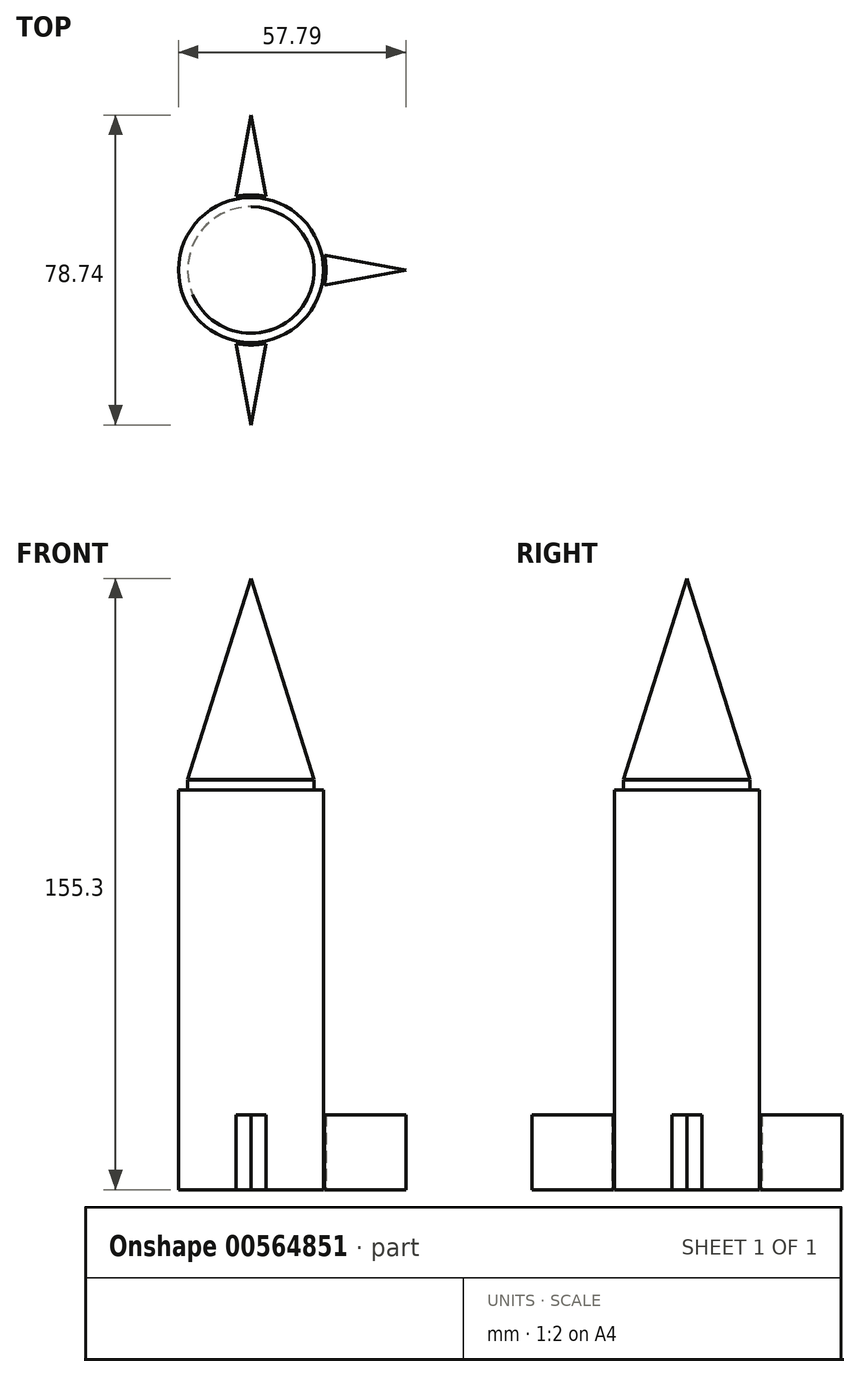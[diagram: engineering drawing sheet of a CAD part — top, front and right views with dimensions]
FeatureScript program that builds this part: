
annotation { "Feature Type Name" : "Feature", "Feature Type Description" : "" }
export const myFeature = defineFeature(function(context is Context, id is Id, definition is map)
    precondition{}
    {
        {
            var Q0;
            Q0=qCreatedBy(makeId("Top.planeOp"),FACE);
            var sketch = newSketch(context, id + "F0", { "sketchPlane" : qUnion([Q0])});
            skCircle(sketch, "E0", {"center": v(0, 0) * mm, "radius": 19.05 * mm});
            skPoint(sketch, "E1", {"position": v(-18.67, 3.81) * mm});
            skPoint(sketch, "E2", {"position": v(-18.67, -3.81) * mm});
            skPoint(sketch, "E3", {"position": v(-19.05, 0) * mm});
            skPoint(sketch, "E4", {"position": v(-39.37, 0) * mm});
            skLineSegment(sketch, "E5", {"start": v(-18.67, -3.8) * mm, "end": v(-39.37, 0) * mm});
            skLineSegment(sketch, "E6", {"start": v(-18.67, 3.8) * mm, "end": v(-39.37, 0) * mm});
            skPoint(sketch, "E7", {"position": v(-3.81, -18.67) * mm});
            skPoint(sketch, "E8", {"position": v(3.81, -18.67) * mm});
            skPoint(sketch, "E9", {"position": v(0, -19.05) * mm});
            skPoint(sketch, "E10", {"position": v(0, -39.37) * mm});
            skLineSegment(sketch, "E11", {"start": v(-3.81, -18.67) * mm, "end": v(0, -39.37) * mm});
            skLineSegment(sketch, "E12", {"start": v(3.81, -18.67) * mm, "end": v(0, -39.37) * mm});
            skLineSegment(sketch, "E13.MirrorCS", {"start": v(-18.67, 3.81) * mm, "end": v(-39.37, 0) * mm});
            skLineSegment(sketch, "E14.MirrorCS", {"start": v(-18.67, -3.81) * mm, "end": v(-39.37, 0) * mm});
            skLineSegment(sketch, "E15.MirrorCS", {"start": v(-3.81, 18.67) * mm, "end": v(0, 39.37) * mm});
            skLineSegment(sketch, "E16.MirrorCS", {"start": v(3.81, 18.67) * mm, "end": v(0, 39.37) * mm});
            skPoint(sketch, "E17.MirrorP", {"position": v(-3.81, 18.67) * mm});
            skPoint(sketch, "E18.MirrorP", {"position": v(0, 19.05) * mm});
            skPoint(sketch, "E19.MirrorP", {"position": v(3.81, 18.67) * mm});
            skPoint(sketch, "E20.MirrorP", {"position": v(0, 39.37) * mm});
            skLineSegment(sketch, "E21.MirrorCS", {"start": v(18.67, 3.81) * mm, "end": v(39.37, 0) * mm});
            skLineSegment(sketch, "E22.MirrorCS", {"start": v(18.67, -3.81) * mm, "end": v(39.37, 0) * mm});
            skPoint(sketch, "E23.MirrorP", {"position": v(39.37, 0) * mm});
            skPoint(sketch, "E24.MirrorP", {"position": v(18.67, 3.81) * mm});
            skPoint(sketch, "E25.MirrorP", {"position": v(19.05, 0) * mm});
            skPoint(sketch, "E26", {"position": v(18.67, -3.81) * mm});
            skSolve(sketch);
        }
        {
            var Q0;
            {var subQ0=sQuery(id+"F0.wireOp",EDGE,"E14.MirrorCS");Q0=makeQuery(id+"F0.imprint","IMPRINT",FACE,{"disambiguationData":[TD([[makeQuery(id+"F0.imprint","IMPRINT",EDGE,{"derivedFrom":subQ0}),-1.0]])]});}
            var Q1;
            {var subQ0=sQuery(id+"F0.wireOp",EDGE,"E0");var subQ5=makeQuery(id+"F0.imprint","INTERSECT",VERTEX,{"derivedFrom":[sQuery(id+"F0.wireOp",EDGE,"E13.MirrorCS"),subQ0]});Q1=makeQuery(id+"F0.imprint","IMPRINT",FACE,{"disambiguationData":[TD([[makeQuery(id+"F0.imprint","IMPRINT",EDGE,{"disambiguationData":[TD([[subQ5,-1.0]])],"derivedFrom":subQ0}),-1.0]])]});}
            var Q2;
            {var subQ0=sQuery(id+"F0.wireOp",EDGE,"E11");Q2=makeQuery(id+"F0.imprint","IMPRINT",FACE,{"disambiguationData":[TD([[makeQuery(id+"F0.imprint","IMPRINT",EDGE,{"derivedFrom":subQ0}),1.0]])]});}
            var Q3;
            {var subQ0=sQuery(id+"F0.wireOp",EDGE,"E21.MirrorCS");Q3=makeQuery(id+"F0.imprint","IMPRINT",FACE,{"disambiguationData":[TD([[makeQuery(id+"F0.imprint","IMPRINT",EDGE,{"derivedFrom":subQ0}),-1.0]])]});}
            var Q4;
            {var subQ0=sQuery(id+"F0.wireOp",EDGE,"E15.MirrorCS");Q4=makeQuery(id+"F0.imprint","IMPRINT",FACE,{"disambiguationData":[TD([[makeQuery(id+"F0.imprint","IMPRINT",EDGE,{"derivedFrom":subQ0}),-1.0]])]});}
            extrude(context, id + "F1", {"entities" : qUnion([Q0, Q1, Q2, Q3, Q4]), "depth" : 19.05 * mm, "offsetDistance" : 25.4 * mm});
        }
        {
            var Q0;
            Q0=qCreatedBy(makeId("Top.planeOp"),FACE);
            var sketch = newSketch(context, id + "F2", { "sketchPlane" : qUnion([Q0])});
            skCircle(sketch, "E27", {"center": v(0, 0) * mm, "radius": 18.41 * mm});
            skSolve(sketch);
        }
        {
            var Q0;
            Q0=makeQuery(id+"F2.imprint","IMPRINT",FACE,{"disambiguationData":[TD([[makeQuery(id+"F2.imprint","IMPRINT",EDGE,{"derivedFrom":sQuery(id+"F2.wireOp",EDGE,"E27")}),1.0]])]});
            extrude(context, id + "F3", {"entities" : qUnion([Q0]), "operationType" : NewBodyOperationType.ADD, "depth" : 101.6 * mm, "offsetDistance" : 25.4 * mm});
        }
        {
            var Q0;
            Q0=qCreatedBy(makeId("Top.planeOp"),FACE);
            var sketch = newSketch(context, id + "F4", { "sketchPlane" : qUnion([Q0])});
            skCircle(sketch, "E28", {"center": v(0, 0) * mm, "radius": 16.06 * mm});
            skSolve(sketch);
        }
        {
            var Q0;
            Q0=makeQuery(id+"F4.imprint","IMPRINT",FACE,{"disambiguationData":[TD([[makeQuery(id+"F4.imprint","IMPRINT",EDGE,{"derivedFrom":sQuery(id+"F4.wireOp",EDGE,"E28")}),1.0]])]});
            extrude(context, id + "F5", {"entities" : qUnion([Q0]), "operationType" : NewBodyOperationType.ADD, "depth" : 104.14 * mm, "offsetDistance" : 25.4 * mm});
        }
        {
            var Q0;
            Q0=qCreatedBy(makeId("Right.planeOp"),FACE);
            var sketch = newSketch(context, id + "F6", { "sketchPlane" : qUnion([Q0])});
            skPoint(sketch, "E29", {"position": v(-16.05, 104.17) * mm});
            skPoint(sketch, "E30", {"position": v(16.09, 104.17) * mm});
            skPoint(sketch, "E31", {"position": v(0.02, 104.17) * mm});
            skPoint(sketch, "E32", {"position": v(0, 155.3) * mm});
            skLineSegment(sketch, "E33", {"start": v(0, 155.3) * mm, "end": v(0.02, 104.17) * mm});
            skLineSegment(sketch, "E34", {"start": v(0.02, 104.17) * mm, "end": v(-16.05, 104.17) * mm});
            skLineSegment(sketch, "E35", {"start": v(0, 155.3) * mm, "end": v(-16.05, 104.17) * mm});
            skSolve(sketch);
        }
        {
            var Q0;
            Q0=makeQuery(id+"F6.imprint","IMPRINT",FACE,{"disambiguationData":[TD([[makeQuery(id+"F6.imprint","IMPRINT",EDGE,{"derivedFrom":sQuery(id+"F6.wireOp",EDGE,"E33")}),-1.0]])]});
            var Q1;
            Q1=sQuery(id+"F6.wireOp",EDGE,"E33");
            revolve(context, id + "F7", {"entities" : qUnion([Q0]), "axis" : qUnion([Q1]), "revolveType" : RevolveType.FULL});
        }
    });
